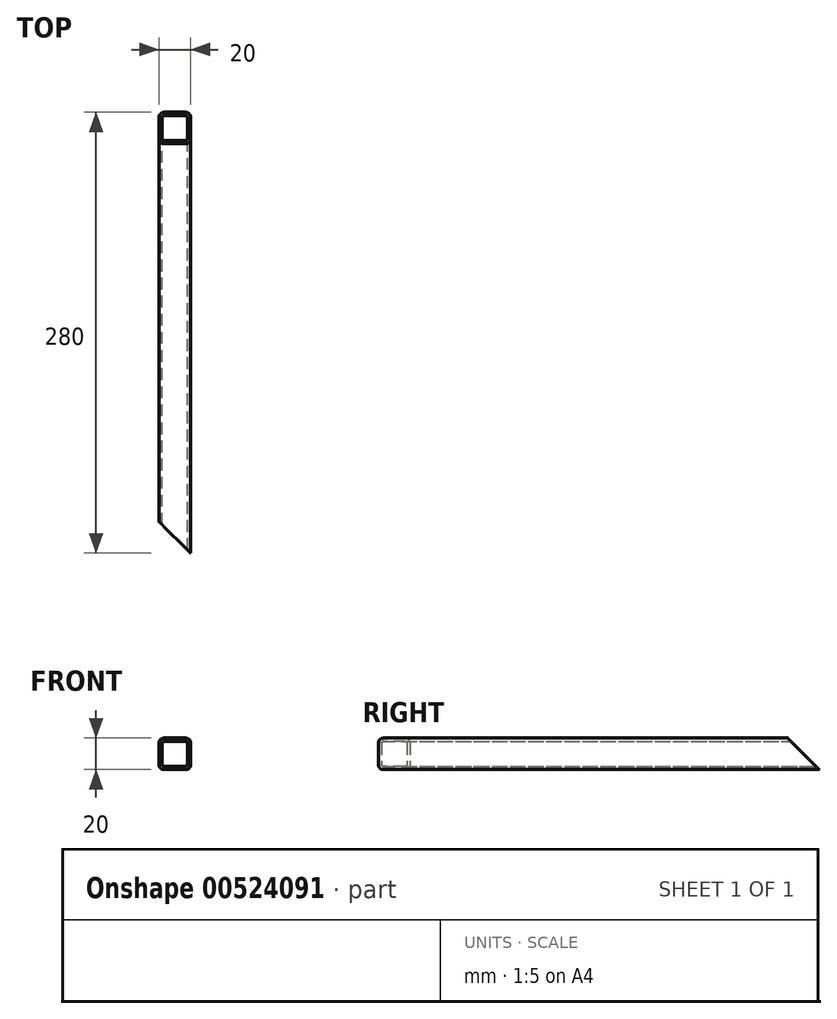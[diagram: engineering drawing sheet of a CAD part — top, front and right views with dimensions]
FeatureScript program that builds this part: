
annotation { "Feature Type Name" : "Feature", "Feature Type Description" : "" }
export const myFeature = defineFeature(function(context is Context, id is Id, definition is map)
    precondition{}
    {
        {
            assignVariable(context, id + "F0", {"name" : "R", "anyValue" : 3});
        }
        {
            assignVariable(context, id + "F1", {"name" : "W", "anyValue" : 2});
        }
        {
            var Q0;
            Q0=qCreatedBy(makeId("Front.planeOp"),FACE);
            var sketch = newSketch(context, id + "F2", { "sketchPlane" : qUnion([Q0])});
            skLineSegment(sketch, "E0.bottom", {"start": v(-10, 10) * mm, "end": v(10, 10) * mm});
            skLineSegment(sketch, "E0.top", {"start": v(-10, -10) * mm, "end": v(10, -10) * mm});
            skLineSegment(sketch, "E0.left", {"start": v(-10, 10) * mm, "end": v(-10, -10) * mm});
            skLineSegment(sketch, "E0.right", {"start": v(10, 10) * mm, "end": v(10, -10) * mm});
            skSolve(sketch);
        }
        {
            var Q0;
            Q0=qSketchRegion(id+"F2",true);
            extrude(context, id + "F3", {"entities" : qUnion([Q0]), "endBound" : BoundingType.SYMMETRIC, "depth" : 280 * mm, "offsetDistance" : 25 * mm});
        }
        {
            var Q0;
            Q0=makeQuery(id+"F3.opExtrude","SWEPT_EDGE",EDGE,{"disambiguationData":[OSD([sQuery(id+"F2.wireOp",EDGE,"E0.bottom"),sQuery(id+"F2.wireOp",EDGE,"E0.right")])]});
            var Q1;
            Q1=makeQuery(id+"F3.opExtrude","SWEPT_EDGE",EDGE,{"disambiguationData":[OSD([sQuery(id+"F2.wireOp",EDGE,"E0.bottom"),sQuery(id+"F2.wireOp",EDGE,"E0.left")])]});
            var Q2;
            Q2=makeQuery(id+"F3.opExtrude","SWEPT_EDGE",EDGE,{"disambiguationData":[OSD([sQuery(id+"F2.wireOp",EDGE,"E0.top"),sQuery(id+"F2.wireOp",EDGE,"E0.right")])]});
            var Q3;
            Q3=makeQuery(id+"F3.opExtrude","SWEPT_EDGE",EDGE,{"disambiguationData":[OSD([sQuery(id+"F2.wireOp",EDGE,"E0.top"),sQuery(id+"F2.wireOp",EDGE,"E0.left")])]});
            fillet(context, id + "F4", {"entities" : qUnion([Q0, Q1, Q2, Q3]), "radius" : (getVariable(context, 'R')) * mm, "tangentPropagation" : true, "allowEdgeOverflow" : false});
        }
        {
            var Q0;
            Q0=makeQuery(id+"F3.opExtrude","CAP_FACE",FACE,{"disambiguationData":[OSD([sQuery(id+"F2.wireOp",EDGE,"E0.bottom"),sQuery(id+"F2.wireOp",EDGE,"E0.top"),sQuery(id+"F2.wireOp",EDGE,"E0.left"),sQuery(id+"F2.wireOp",EDGE,"E0.right")])],"isStart":false});
            var Q1;
            Q1=makeQuery(id+"F3.opExtrude","CAP_FACE",FACE,{"disambiguationData":[OSD([sQuery(id+"F2.wireOp",EDGE,"E0.bottom"),sQuery(id+"F2.wireOp",EDGE,"E0.top"),sQuery(id+"F2.wireOp",EDGE,"E0.left"),sQuery(id+"F2.wireOp",EDGE,"E0.right")])],"isStart":true});
            shell(context, id + "F5", {"entities" : qUnion([Q0, Q1]), "thickness" : (getVariable(context, 'W')) * mm});
        }
        {
            var Q0;
            Q0=makeQuery(id+"F3.opExtrude","SWEPT_FACE",FACE,{"disambiguationData":[OSD([sQuery(id+"F2.wireOp",EDGE,"E0.left")])]});
            var sketch = newSketch(context, id + "F6", { "sketchPlane" : qUnion([Q0])});
            skLineSegment(sketch, "E1", {"start": v(-140, 10) * mm, "end": v(-140, -10) * mm});
            skLineSegment(sketch, "E2.0", {"start": v(-140, 10) * mm, "end": v(-120, 10) * mm});
            skLineSegment(sketch, "E3", {"start": v(-140, -10) * mm, "end": v(-120, 10) * mm});
            skPoint(sketch, "E4.orphan", {"position": v(140, 10) * mm});
            skSolve(sketch);
        }
        {
            var Q0;
            Q0=qSketchRegion(id+"F6",true);
            extrude(context, id + "F7", {"entities" : qUnion([Q0]), "operationType" : NewBodyOperationType.REMOVE, "endBound" : BoundingType.THROUGH_ALL, "oppositeDirection" : true, "depth" : 25 * mm, "offsetDistance" : 25 * mm});
        }
        {
            var Q0;
            Q0=makeQuery(id+"F3.opExtrude","SWEPT_FACE",FACE,{"disambiguationData":[OSD([sQuery(id+"F2.wireOp",EDGE,"E0.top")])]});
            var sketch = newSketch(context, id + "F8", { "sketchPlane" : qUnion([Q0])});
            skLineSegment(sketch, "E5.0", {"start": v(10, 140) * mm, "end": v(10, -137) * mm, "construction": true});
            skLineSegment(sketch, "E6.0", {"start": v(-10, -137) * mm, "end": v(-10, 140) * mm, "construction": true});
            skLineSegment(sketch, "E7", {"start": v(-10, 140) * mm, "end": v(10, 140) * mm});
            skLineSegment(sketch, "E8", {"start": v(10, 140) * mm, "end": v(-10, 120) * mm});
            skLineSegment(sketch, "E9", {"start": v(-10, 120) * mm, "end": v(-10, 140) * mm});
            skSolve(sketch);
        }
        {
            var Q0;
            Q0=qSketchRegion(id+"F8",true);
            extrude(context, id + "F9", {"entities" : qUnion([Q0]), "operationType" : NewBodyOperationType.REMOVE, "oppositeDirection" : true, "depth" : 25 * mm, "offsetDistance" : 25 * mm});
        }
    });
